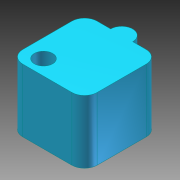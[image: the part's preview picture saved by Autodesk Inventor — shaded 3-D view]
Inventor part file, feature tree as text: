
AUTODESK INVENTOR PART (.ipt)
format: ipt  version: 2012 (Build 160160000, 160)  size: 98,304 bytes
history: native  units: mm
features: extrude x2, sketch x1, fillet x1
ambient origin geometry x8: Origin, YZ Plane, XZ Plane, XY Plane, X Axis, Y Axis, Z Axis, Center Point
bodies: Solid1 (feature_tree)
feature tree (4):
  sketch  "Sketch1"  dims[d0=11.8mm d1=11.8mm d3=5.9mm d4=5.9mm d5=10.0mm d6=0.0mm d7=2.0mm d10=3.5mm d11=2.5mm d12=0.0mm d13=2.9mm d14=3.0mm d15=3.5mm]
  extrude  "Extrusion1"  Depth=11.8mm
  fillet  "Fillet1"  Radius=5.9mm
  extrude  "Extrusion2"  Depth=5.9mm
